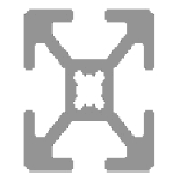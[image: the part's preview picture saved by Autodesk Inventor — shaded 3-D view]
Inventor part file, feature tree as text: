
AUTODESK INVENTOR PART (.ipt)
format: ipt  version: 2013 SP2 (Build 170200200, 200)  size: 235,008 bytes
history: native  units: in
note: dims shown in document units (in); Inventor stores cm internally (conversion verified against a paired STEP export)
features: other x5, sketch x3, plane x1
ambient origin geometry x8: Origin, YZ Plane, XZ Plane, XY Plane, X Axis, Y Axis, Z Axis, Center Point
bodies: Solid1 (feature_tree), Body (feature_tree)
feature tree (9):
  other  "Driven Length"
  other  "Frame Generator"
  other  "Blocks"
  other  "Start Plane"
  other  "End Plane"
  sketch  "Sketch"  dims[d4=0.13in d5=0.0in d6=90.0deg d7=11.0236in]
  sketch  "Sketch2"  dims[d2=0.7874in]
  plane  "Work Plane3"
  sketch  "Sketch3"  dims[d3=11.811in]
